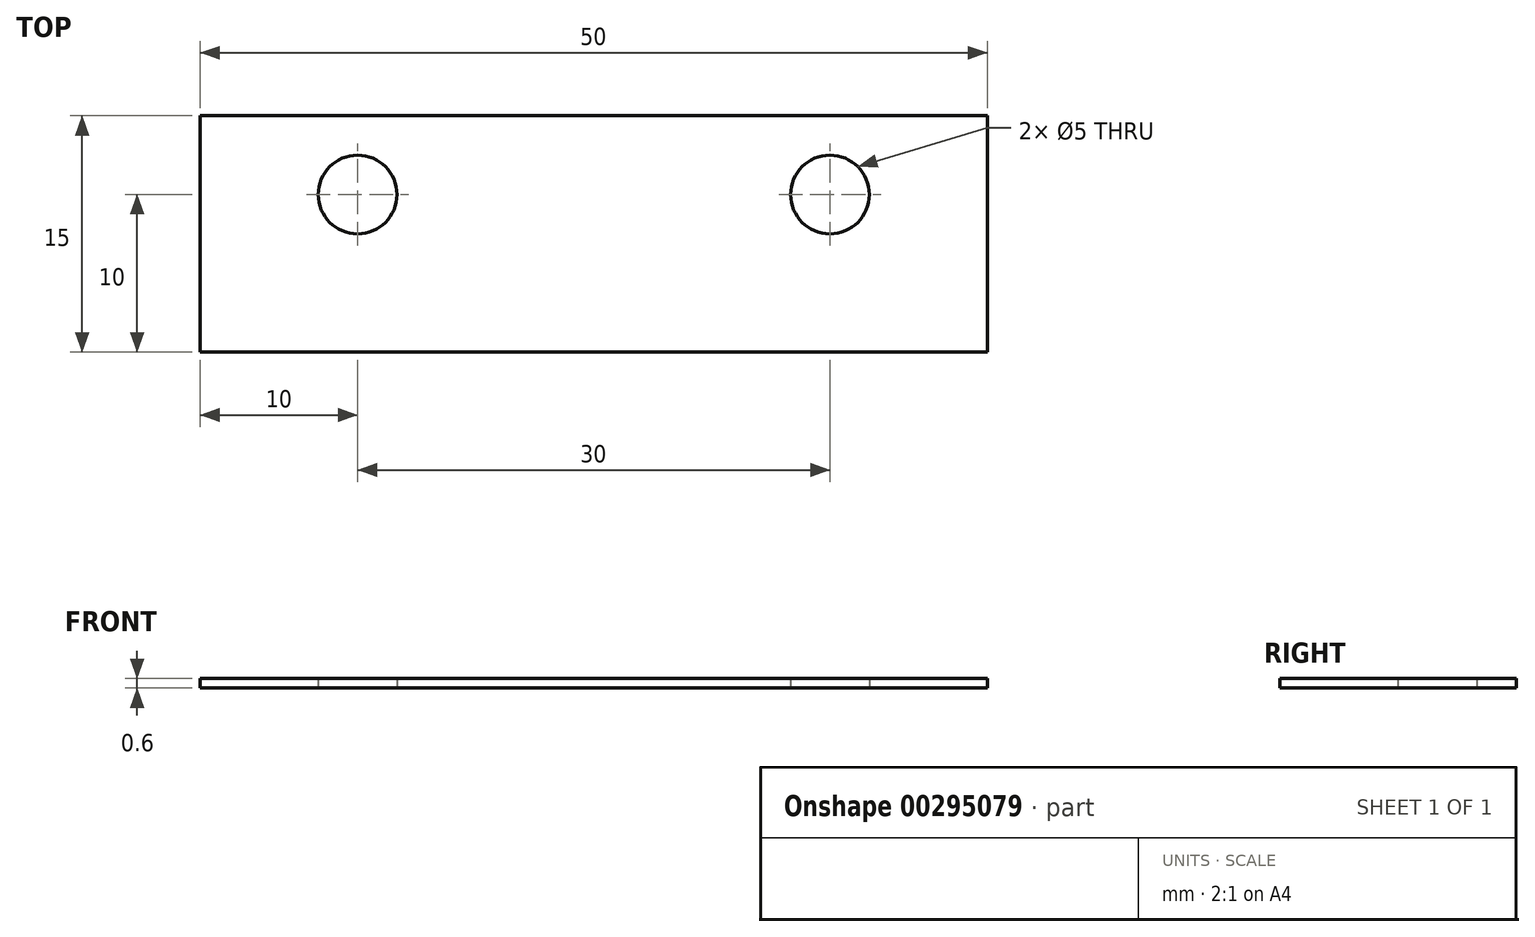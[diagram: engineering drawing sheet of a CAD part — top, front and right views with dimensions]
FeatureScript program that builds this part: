
annotation { "Feature Type Name" : "Feature", "Feature Type Description" : "" }
export const myFeature = defineFeature(function(context is Context, id is Id, definition is map)
    precondition{}
    {
        {
            var Q0;
            Q0=qCreatedBy(makeId("Top.planeOp"),FACE);
            var sketch = newSketch(context, id + "F0", { "sketchPlane" : qUnion([Q0])});
            skLineSegment(sketch, "E0.bottom", {"start": v(25, -7.5) * mm, "end": v(-25, -7.5) * mm});
            skLineSegment(sketch, "E0.top", {"start": v(25, 7.5) * mm, "end": v(-25, 7.5) * mm});
            skLineSegment(sketch, "E0.left", {"start": v(25, -7.5) * mm, "end": v(25, 7.5) * mm});
            skLineSegment(sketch, "E0.right", {"start": v(-25, -7.5) * mm, "end": v(-25, 7.5) * mm});
            skPoint(sketch, "E0.middle", {"position": v(0, 0) * mm});
            skCircle(sketch, "E1", {"center": v(-15, 2.5) * mm, "radius": 2.5 * mm});
            skCircle(sketch, "E2", {"center": v(15, 2.5) * mm, "radius": 2.5 * mm});
            skSolve(sketch);
        }
        {
            var Q0;
            Q0 = qSketchRegion(id + "F0", true);
            extrude(context, id + "F1", {"entities" : qUnion([Q0]), "depth" : 0.6 * mm});
        }
    });
